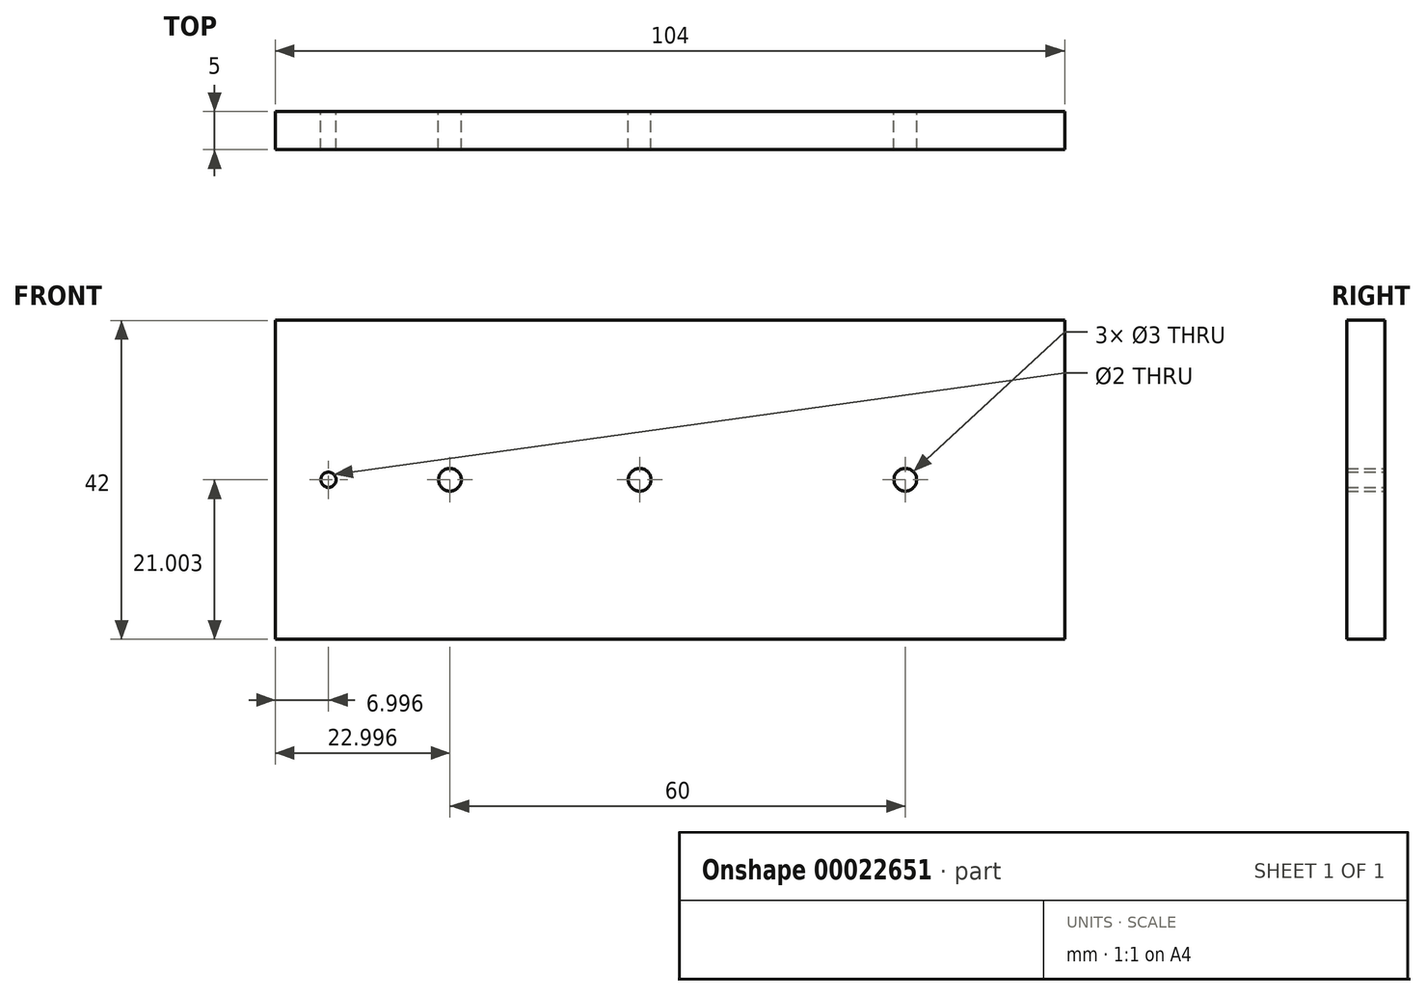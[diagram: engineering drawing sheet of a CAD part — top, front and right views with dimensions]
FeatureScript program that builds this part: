
annotation { "Feature Type Name" : "Feature", "Feature Type Description" : "" }
export const myFeature = defineFeature(function(context is Context, id is Id, definition is map)
    precondition{}
    {
        {
            var Q0;
            Q0=qCreatedBy(makeId("Front.planeOp"),FACE);
            var sketch = newSketch(context, id + "F0", { "sketchPlane" : qUnion([Q0])});
            skLineSegment(sketch, "E0.bottom", {"start": v(-48.77, 14.52) * mm, "end": v(55.23, 14.52) * mm});
            skLineSegment(sketch, "E0.top", {"start": v(-48.77, -27.48) * mm, "end": v(55.23, -27.48) * mm});
            skLineSegment(sketch, "E0.left", {"start": v(-48.77, 14.52) * mm, "end": v(-48.77, -27.48) * mm});
            skLineSegment(sketch, "E0.right", {"start": v(55.23, 14.52) * mm, "end": v(55.23, -27.48) * mm});
            skPoint(sketch, "E1", {"position": v(55.23, -6.48) * mm});
            skCircle(sketch, "E2", {"center": v(34.23, -6.48) * mm, "radius": 1.5 * mm});
            skCircle(sketch, "E3", {"center": v(-25.77, -6.48) * mm, "radius": 1.5 * mm});
            skCircle(sketch, "E4", {"center": v(-0.77, -6.48) * mm, "radius": 1.5 * mm});
            skCircle(sketch, "E5", {"center": v(-41.77, -6.48) * mm, "radius": 1 * mm});
            skSolve(sketch);
        }
        {
            var Q0;
            Q0=makeQuery(id+"F0.imprint","IMPRINT",FACE,{"disambiguationData":[TD([[makeQuery(id+"F0.imprint","IMPRINT",EDGE,{"derivedFrom":sQuery(id+"F0.wireOp",EDGE,"E0.bottom")}),-1.0]])]});
            extrude(context, id + "F1", {"entities" : qUnion([Q0]), "depth" : 5 * mm});
        }
    });
